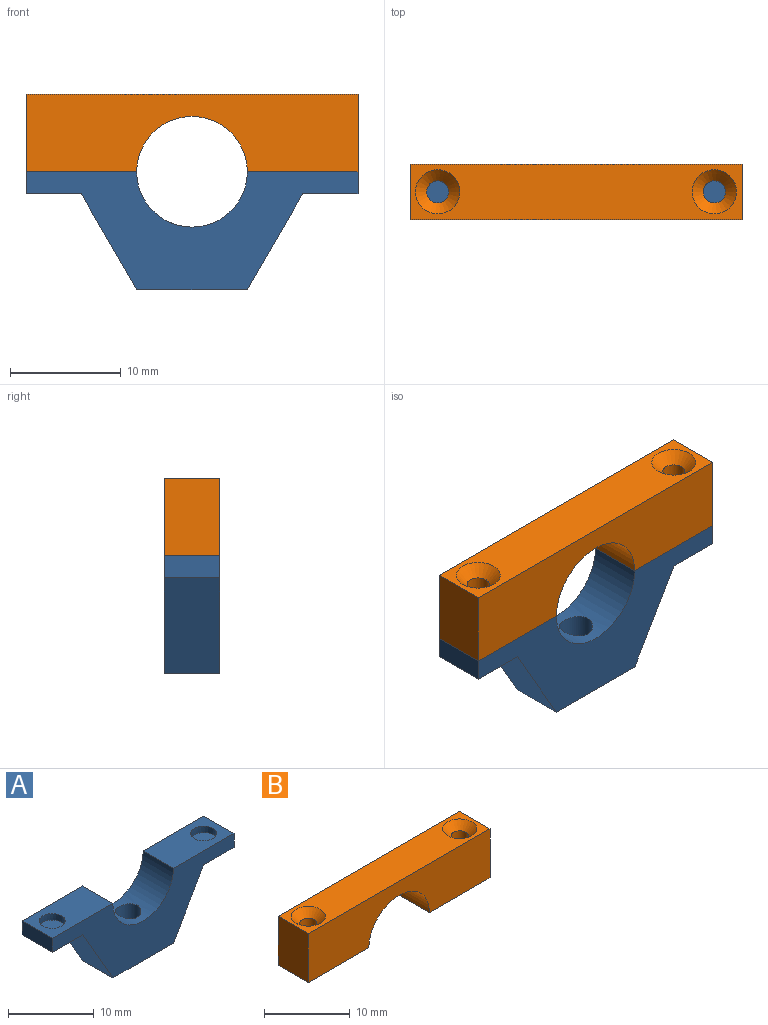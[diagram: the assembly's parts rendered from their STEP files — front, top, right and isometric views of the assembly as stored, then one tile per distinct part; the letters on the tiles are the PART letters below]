
ASSEMBLY  parts=2 mates=1
PART A: 17 faces, bbox 30x5x10.7 mm
  f0: plane 5x2mm, normal (-1,0,0), area 10mm2, adj f1,f9,f10,f11
  f1: plane 5x5mm, normal (0,0,-1), area 25mm2, adj f0,f2,f10,f11
  f2: plane 8.66x5mm, normal (-0.87,0,-0.5), area 50mm2, adj f1,f3,f10,f11
  f3: plane 10x5mm, normal (0,0,-1), area 42.9mm2, adj f2,f4,f10,f11,f16
  f4: plane 8.66x5mm, normal (0.87,0,-0.5), area 50mm2, adj f3,f5,f10,f11
  f5: plane 5x5mm, normal (0,0,-1), area 25mm2, adj f4,f6,f10,f11
  f6: plane 5x2mm, normal (1,0,0), area 10mm2, adj f5,f7,f10,f11
  f7: plane 10x5mm, normal (0,0,1), area 42.9mm2, adj f6,f8,f10,f11,f14
  f8: cylinder r=5mm len=10mm, axis (0,1,0), area 71.4mm2, adj f7,f9,f10,f11,f16
  f9: plane 10x5mm, normal (0,0,1), area 42.9mm2, adj f0,f8,f10,f11,f12
  f10: plane 30x10.66mm, normal (0,-1,0), area 150.6mm2, adj f0,f1,f2,f3,f4,f5,f6,f7
  f11: plane 30x10.66mm, normal (0,1,0), area 150.6mm2, adj f0,f1,f2,f3,f4,f5,f6,f7
  f12: cone r=1.5mm half-angle=5deg, axis (0,0,-1), area 9.7mm2, adj f9,f13
  f13: plane 3.18x3.18mm, normal (0,0,1), area 7.9mm2, adj f12
  f14: cone r=1.5mm half-angle=5deg, axis (0,0,-1), area 9.7mm2, adj f7,f15
  f15: plane 3.18x3.18mm, normal (0,0,1), area 7.9mm2, adj f14
  f16: cylinder r=1.5mm len=5.89mm, axis (0,0,1), area 54.4mm2, adj f3,f8
PART B: 12 faces, bbox 30x5x7 mm
  f0: plane 30x5mm, normal (0,0,1), area 124.9mm2, adj f1,f5,f6,f7,f10,f11
  f1: plane 7x5mm, normal (-1,0,0), area 35mm2, adj f0,f2,f6,f7
  f2: plane 10x5mm, normal (0,0,-1), area 46.9mm2, adj f1,f3,f6,f7,f8
  f3: cylinder r=5mm len=10mm, axis (0,1,0), area 78.5mm2, adj f2,f4,f6,f7
  f4: plane 10x5mm, normal (0,0,-1), area 46.9mm2, adj f3,f5,f6,f7,f9
  f5: plane 7x5mm, normal (1,0,0), area 35mm2, adj f0,f4,f6,f7
  f6: plane 30x7mm, normal (0,-1,0), area 170.7mm2, adj f0,f1,f2,f3,f4,f5
  f7: plane 30x7mm, normal (0,1,0), area 170.7mm2, adj f0,f1,f2,f3,f4,f5
  f8: cylinder r=1mm len=6mm, axis (0,0,1), area 37.7mm2, adj f2,f11
  f9: cylinder r=1mm len=6mm, axis (0,0,1), area 37.7mm2, adj f4,f10
  f10: cone r=1.5mm half-angle=45deg, axis (0,0,1), area 13.3mm2, adj f0,f9
  f11: cone r=1.5mm half-angle=45deg, axis (0,0,1), area 13.3mm2, adj f0,f8
PLACE A t=(-8.71,18.85,27.94)mm
PLACE B t=(-8.71,21.35,27.94)mm
MATE fastened A.f12 <-> B.f11  axis (0,0,1) through (-21.21,18.85,27.94)mm
